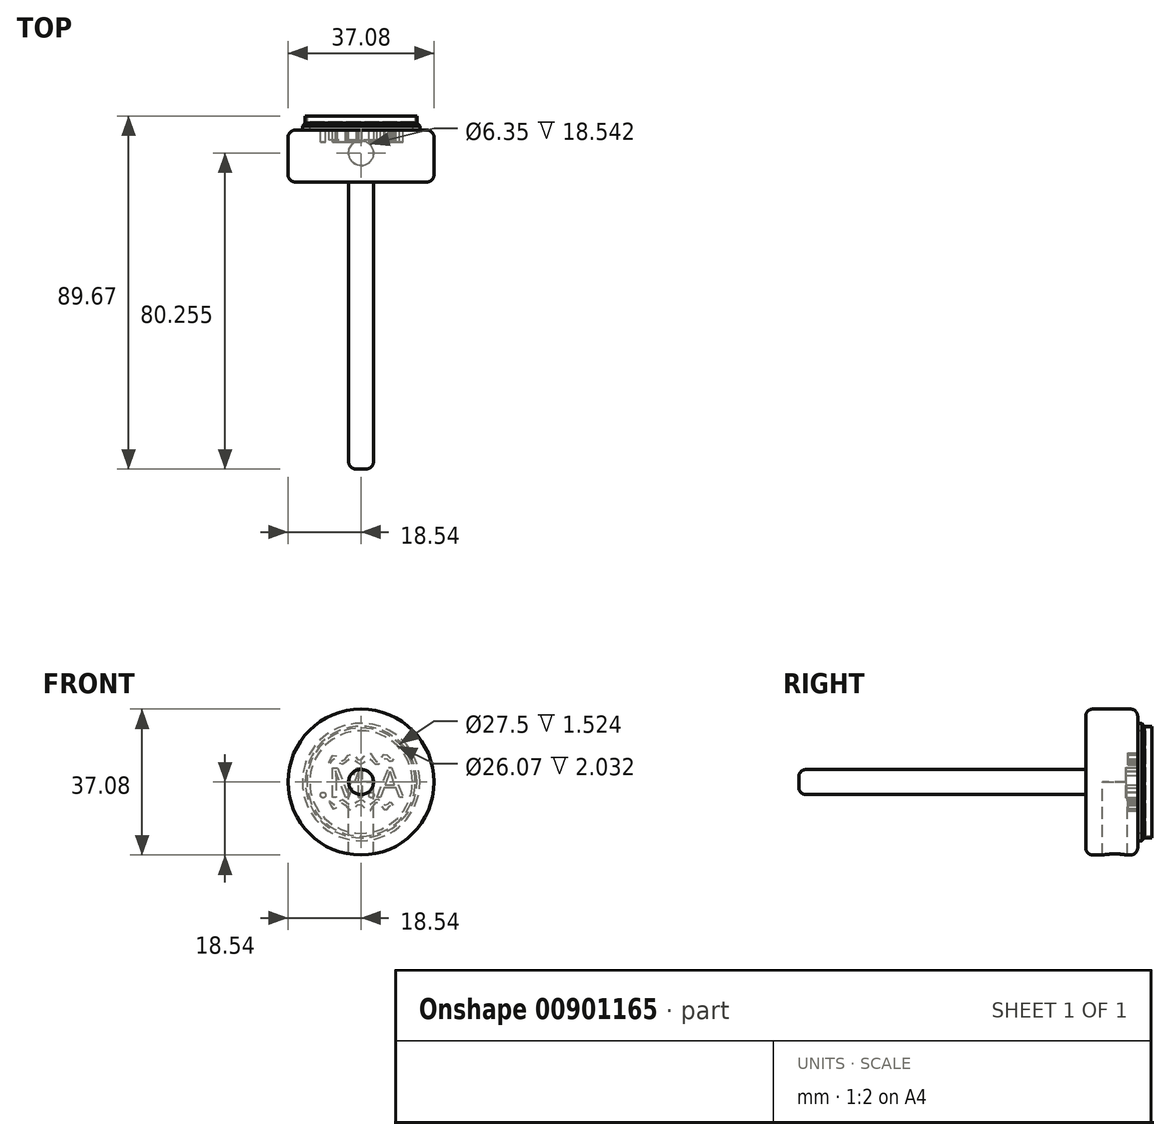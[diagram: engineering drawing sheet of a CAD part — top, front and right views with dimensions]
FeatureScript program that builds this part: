
annotation { "Feature Type Name" : "Feature", "Feature Type Description" : "" }
export const myFeature = defineFeature(function(context is Context, id is Id, definition is map)
    precondition{}
    {
        {
            var Q0;
            Q0=qCreatedBy(makeId("Front.planeOp"),FACE);
            var sketch = newSketch(context, id + "F0", { "sketchPlane" : qUnion([Q0])});
            skCircle(sketch, "E0", {"center": v(0, 0) * mm, "radius": 18.54 * mm});
            skSolve(sketch);
        }
        {
            var Q0;
            Q0 = qSketchRegion(id + "F0", true);
            extrude(context, id + "F1", {"entities" : qUnion([Q0]), "depth" : 13.2 * mm, "offsetDistance" : 25.4 * mm});
        }
        {
            var Q0;
            Q0=qCreatedBy(makeId("Front.planeOp"),FACE);
            var sketch = newSketch(context, id + "F2", { "sketchPlane" : qUnion([Q0])});
            skCircle(sketch, "E1", {"center": v(0, 0) * mm, "radius": 3.18 * mm});
            skSolve(sketch);
        }
        {
            var Q0;
            Q0=makeQuery(id+"F2.imprint","IMPRINT",FACE,{"disambiguationData":[TD([[makeQuery(id+"F2.imprint","IMPRINT",EDGE,{"derivedFrom":sQuery(id+"F2.wireOp",EDGE,"E1")}),1.0]])]});
            extrude(context, id + "F3", {"entities" : qUnion([Q0]), "operationType" : NewBodyOperationType.ADD, "depth" : 86.1 * mm, "offsetDistance" : 25.4 * mm});
        }
        {
            var Q0;
            Q0=makeQuery(id+"F3.opExtrude","CAP_EDGE",EDGE,{"disambiguationData":[OSD([sQuery(id+"F2.wireOp",EDGE,"E1")])],"isStart":false});
            fillet(context, id + "F4", {"entities" : qUnion([Q0]), "radius" : 1.84 * mm, "tangentPropagation" : true, "allowEdgeOverflow" : false});
        }
        {
            var Q0;
            Q0=makeQuery(id+"F1.opExtrude","CAP_EDGE",EDGE,{"disambiguationData":[OSD([sQuery(id+"F0.wireOp",EDGE,"E0")])],"isStart":false});
            var Q1;
            Q1=makeQuery(id+"F1.opExtrude","CAP_EDGE",EDGE,{"disambiguationData":[OSD([sQuery(id+"F0.wireOp",EDGE,"E0")])],"isStart":true});
            fillet(context, id + "F5", {"entities" : qUnion([Q0, Q1]), "radius" : 1.84 * mm, "tangentPropagation" : true, "allowEdgeOverflow" : false});
        }
        {
            var Q0;
            Q0=qCreatedBy(makeId("Front.planeOp"),FACE);
            var sketch = newSketch(context, id + "F6", { "sketchPlane" : qUnion([Q0])});
            skText(sketch, "E2", { "text": ".M.A", "fontName": "OpenSans-Regular.ttf"});
            skLineSegment(sketch, "E3", {"start": v(15.05, 17.3) * mm, "end": v(72.74, 15.5) * mm});
            skLineSegment(sketch, "E4", {"start": v(72.74, 15.5) * mm, "end": v(87.11, 9.37) * mm});
            const initialGuessF6  = {"E2": [-0.01104, -0.00385, 1, 0, 0.00756]};
            skSetInitialGuess(sketch, initialGuessF6);
            skSolve(sketch);
        }
        {
            var Q0;
            Q0 = qSketchRegion(id + "F6", true);
            extrude(context, id + "F7", {"entities" : qUnion([Q0]), "operationType" : NewBodyOperationType.REMOVE, "depth" : 3.05 * mm, "offsetDistance" : 25.4 * mm});
        }
        {
            var Q0;
            Q0=qCreatedBy(makeId("Front.planeOp"),FACE);
            var sketch = newSketch(context, id + "F8", { "sketchPlane" : qUnion([Q0])});
            skCircle(sketch, "E5", {"center": v(0, 0) * mm, "radius": 13.04 * mm});
            skCircle(sketch, "E6", {"center": v(0, 0) * mm, "radius": 14.92 * mm});
            skSolve(sketch);
        }
        {
            var Q0;
            Q0=makeQuery(id+"F8.imprint","IMPRINT",FACE,{"disambiguationData":[TD([[makeQuery(id+"F8.imprint","IMPRINT",EDGE,{"derivedFrom":sQuery(id+"F8.wireOp",EDGE,"E5")}),-1.0]])]});
            extrude(context, id + "F9", {"entities" : qUnion([Q0]), "operationType" : NewBodyOperationType.ADD, "oppositeDirection" : true, "depth" : 2.03 * mm, "offsetDistance" : 25.4 * mm});
        }
        {
            var Q0;
            Q0=qCreatedBy(makeId("Front.planeOp"),FACE);
            var sketch = newSketch(context, id + "F10", { "sketchPlane" : qUnion([Q0])});
            skCircle(sketch, "E7", {"center": v(0, 0) * mm, "radius": 13.75 * mm});
            skCircle(sketch, "E8", {"center": v(0, 0) * mm, "radius": 14.17 * mm});
            skSolve(sketch);
        }
        {
            var Q0;
            Q0 = qSketchRegion(id + "F10", true);
            extrude(context, id + "F11", {"entities" : qUnion([Q0]), "operationType" : NewBodyOperationType.ADD, "oppositeDirection" : true, "depth" : 3.56 * mm, "offsetDistance" : 25.4 * mm});
        }
        {
            var Q0;
            Q0=makeQuery(id+"F9.opExtrude","CAP_EDGE",EDGE,{"disambiguationData":[OSD([sQuery(id+"F8.wireOp",EDGE,"E6")])],"isStart":false});
            chamfer(context, id + "F12", {"entities" : qUnion([Q0]), "width" : 1.02 * mm, "tangentPropagation" : true});
        }
        {
            var Q0;
            Q0=qCreatedBy(makeId("Front.planeOp"),FACE);
            var sketch = newSketch(context, id + "F13", { "sketchPlane" : qUnion([Q0])});
            skFitSpline(sketch, "E9", {"points": [v(8.27, 5.93) * mm, v(7.36, 5.13) * mm, v(6.24, 5.93) * mm, v(4.04, 4.35) * mm, v(1.98, 5.93) * mm, v(0, 4.48) * mm, v(-2.51, 5.93) * mm, v(-4.95, 4.48) * mm, v(-6.62, 5.93) * mm, v(-8.01, 4.76) * mm, v(-8.14, 5.02) * mm], "startDerivative": vector(-11.34, -16.91) * mm, "endDerivative": vector(-1.63, 11) * mm});
            skFitSpline(sketch, "E10", {"points": [v(-8.14, 5.02) * mm, v(-6.72, 6.82) * mm, v(-4.73, 5.32) * mm, v(-2.55, 7.17) * mm, v(-0.32, 5.58) * mm, v(2.02, 7.45) * mm, v(4.12, 5.02) * mm, v(6.09, 7.07) * mm, v(7.48, 5.9) * mm, v(8.27, 5.93) * mm], "startDerivative": vector(11.93, 26.95) * mm, "endDerivative": vector(12.08, 5.33) * mm});
            skFitSpline(sketch, "E11.MirrorCS", {"points": [v(-8.14, -5.02) * mm, v(-6.72, -6.82) * mm, v(-4.73, -5.32) * mm, v(-2.55, -7.17) * mm, v(-0.32, -5.58) * mm, v(2.02, -7.45) * mm, v(4.12, -5.02) * mm, v(6.09, -7.07) * mm, v(7.48, -5.9) * mm, v(8.27, -5.93) * mm], "startDerivative": vector(11.93, -26.95) * mm, "endDerivative": vector(12.08, -5.33) * mm});
            skFitSpline(sketch, "E12.MirrorCS", {"points": [v(8.27, -5.93) * mm, v(7.36, -5.13) * mm, v(6.24, -5.93) * mm, v(4.04, -4.35) * mm, v(1.98, -5.93) * mm, v(0, -4.48) * mm, v(-2.51, -5.93) * mm, v(-4.95, -4.48) * mm, v(-6.62, -5.93) * mm, v(-8.01, -4.76) * mm, v(-8.14, -5.02) * mm], "startDerivative": vector(-11.34, 16.91) * mm, "endDerivative": vector(-1.63, -11) * mm});
            skSolve(sketch);
        }
        {
            var Q0;
            Q0=makeQuery(id+"F13.imprint","IMPRINT",FACE,{"disambiguationData":[TD([[makeQuery(id+"F13.imprint","IMPRINT",EDGE,{"derivedFrom":sQuery(id+"F13.wireOp",EDGE,"E9")}),-1.0]])]});
            var Q1;
            Q1=makeQuery(id+"F13.imprint","IMPRINT",FACE,{"disambiguationData":[TD([[makeQuery(id+"F13.imprint","IMPRINT",EDGE,{"derivedFrom":sQuery(id+"F13.wireOp",EDGE,"E11.MirrorCS")}),1.0]])]});
            extrude(context, id + "F14", {"entities" : qUnion([Q0, Q1]), "operationType" : NewBodyOperationType.REMOVE, "depth" : 2.54 * mm, "offsetDistance" : 25.4 * mm});
        }
        {
            var Q0;
            Q0=qCreatedBy(makeId("Top.planeOp"),FACE);
            var sketch = newSketch(context, id + "F15", { "sketchPlane" : qUnion([Q0])});
            skCircle(sketch, "E13", {"center": v(0, -5.86) * mm, "radius": 2.6 * mm});
            skSolve(sketch);
        }
        {
            var Q0;
            Q0=sQuery(id+"F15.wireOp",VERTEX,"E13.center");
            var Q1;
            Q1=makeQuery(id+"F1.opExtrude","SWEPT_BODY",BODY,{"disambiguationData":[OSD([sQuery(id+"F0.wireOp",EDGE,"E0")])]});
            hole(context, id + "F16", {"style" : HoleStyle.SIMPLE, "endStyle" : HoleEndStyle.THROUGH, "holeDiameter" : 6.35 * mm, "majorDiameter" : 6.35 * mm, "isTappedThrough" : true, "tappedDepth" : 12.7 * mm, "tapClearance" : 3, "locations" : qUnion([Q0]), "scope" : qUnion([Q1])});
        }
    });
